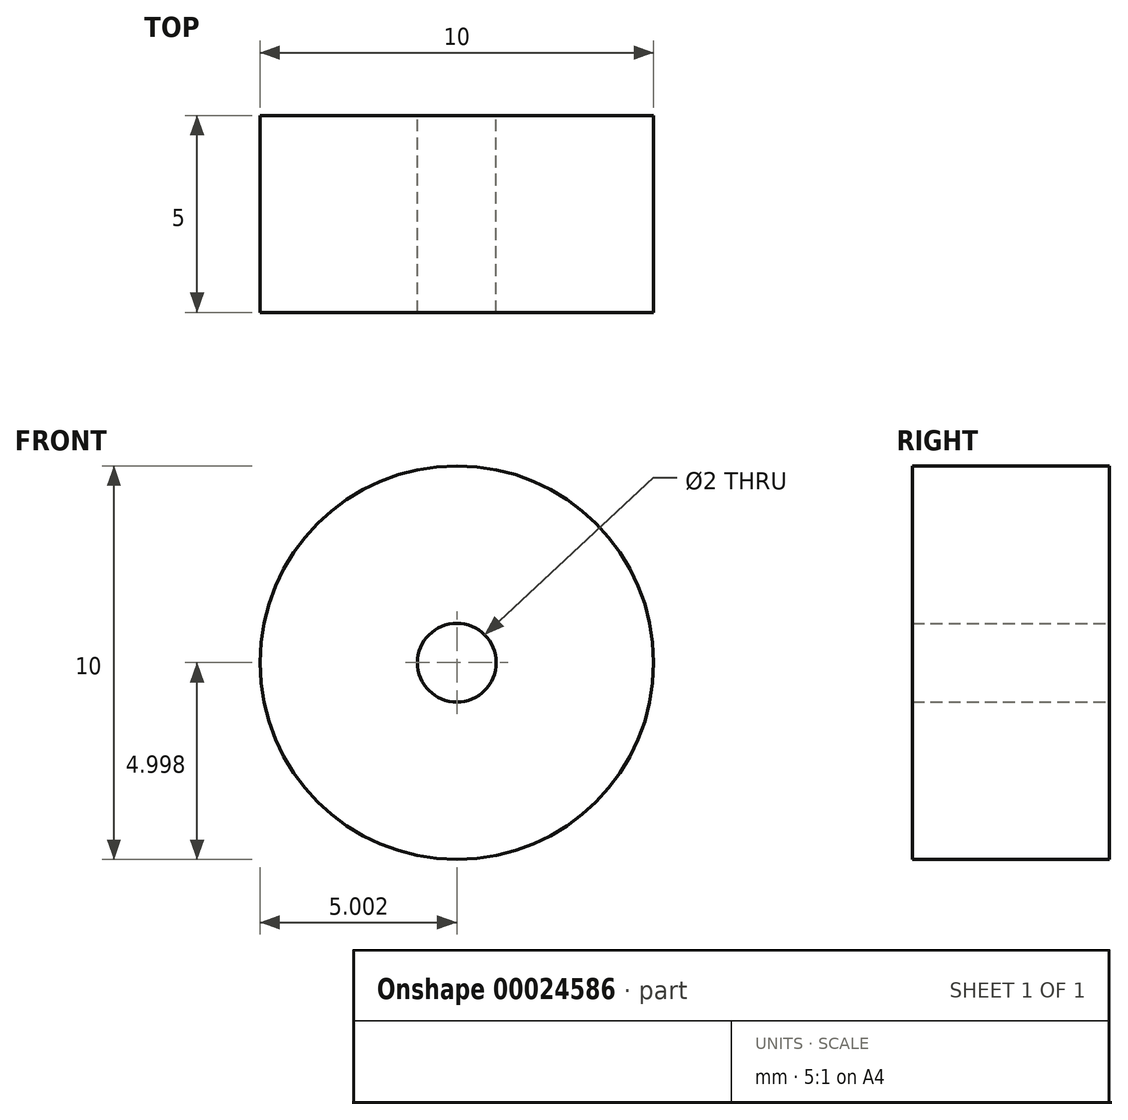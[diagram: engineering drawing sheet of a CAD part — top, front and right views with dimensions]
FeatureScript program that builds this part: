
annotation { "Feature Type Name" : "Feature", "Feature Type Description" : "" }
export const myFeature = defineFeature(function(context is Context, id is Id, definition is map)
    precondition{}
    {
        {
            var Q0;
            Q0=qCreatedBy(makeId("Front.planeOp"),FACE);
            var sketch = newSketch(context, id + "F0", { "sketchPlane" : qUnion([Q0])});
            skCircle(sketch, "E0", {"center": v(-4.7, 4.39) * mm, "radius": 5 * mm});
            skCircle(sketch, "E1", {"center": v(-4.7, 4.39) * mm, "radius": 1 * mm});
            skLineSegment(sketch, "E2", {"start": v(-9.78, 4.79) * mm, "end": v(-9.68, 4.78) * mm});
            skPoint(sketch, "E3.end.orphan", {"position": v(-4.7, 3.39) * mm});
            skLineSegment(sketch, "E4", {"start": v(-4.7, 3.39) * mm, "end": v(-4.7, 5.39) * mm});
            skLineSegment(sketch, "E5", {"start": v(-9.6, 3.44) * mm, "end": v(0.21, 5.34) * mm});
            skSolve(sketch);
        }
        {
            var Q0;
            {var subQ0=sQuery(id+"F0.wireOp",EDGE,"E5");var subQ3=sQuery(id+"F0.wireOp",EDGE,"E0");var subQ6=makeQuery(id+"F0.imprint","INTERSECT",VERTEX,{"disambiguationData":[OD(0.0)],"derivedFrom":[subQ3,subQ0]});Q0=makeQuery(id+"F0.imprint","IMPRINT",FACE,{"disambiguationData":[TD([[makeQuery(id+"F0.imprint","IMPRINT",EDGE,{"disambiguationData":[TD([[subQ6,-1.0]])],"derivedFrom":subQ3}),1.0]])]});}
            var Q1;
            {var subQ3=sQuery(id+"F0.wireOp",EDGE,"E0");var subQ8=makeQuery(id+"F0.imprint","IMPRINT",VERTEX,{"derivedFrom":subQ3});Q1=makeQuery(id+"F0.imprint","IMPRINT",FACE,{"disambiguationData":[TD([[makeQuery(id+"F0.imprint","IMPRINT",EDGE,{"disambiguationData":[TD([[subQ8,1.0]])],"derivedFrom":subQ3}),1.0]])]});}
            extrude(context, id + "F1", {"entities" : qUnion([Q0, Q1]), "depth" : 5 * mm});
        }
    });
